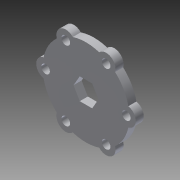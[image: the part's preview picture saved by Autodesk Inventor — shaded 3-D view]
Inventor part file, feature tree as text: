
AUTODESK INVENTOR PART (.ipt)
format: ipt  version: 2013 (Build 170138000, 138)  size: 144,896 bytes
history: native  units: in
note: dims shown in document units (in); Inventor stores cm internally (conversion verified against a paired STEP export)
features: extrude x1, sketch x1, reference x1
ambient origin geometry x8: Origin, YZ Plane, XZ Plane, XY Plane, X Axis, Y Axis, Z Axis, Center Point
bodies: Solid1 (feature_tree)
feature tree (3):
  extrude  "Extrusion1"  Depth=0.1875in TaperAngle=0.0deg
  sketch  "Sketch1"  dims[d0=0.5in d1=0.1875in d2=0.0in]
  reference  "Reference2"
